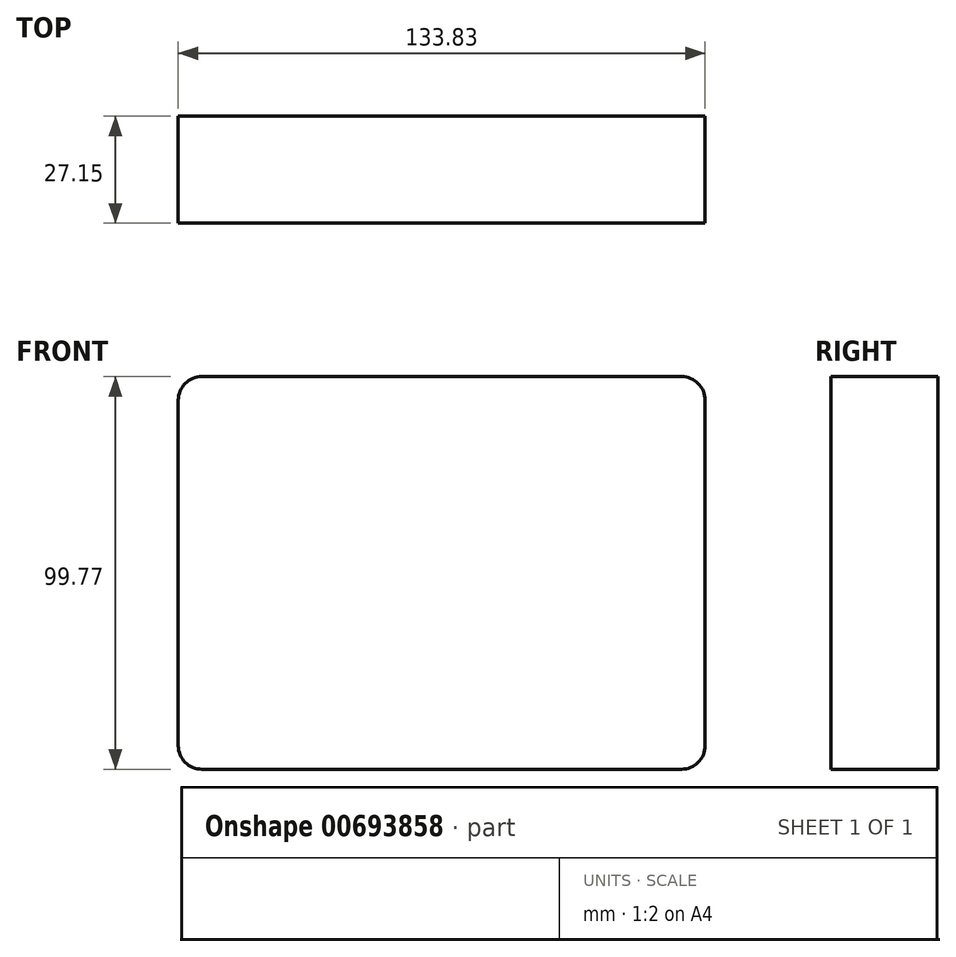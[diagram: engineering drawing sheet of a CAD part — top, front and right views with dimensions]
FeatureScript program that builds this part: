
annotation { "Feature Type Name" : "Feature", "Feature Type Description" : "" }
export const myFeature = defineFeature(function(context is Context, id is Id, definition is map)
    precondition{}
    {
        {
            var Q0;
            Q0=qCreatedBy(makeId("Front.planeOp"),FACE);
            var sketch = newSketch(context, id + "F0", { "sketchPlane" : qUnion([Q0])});
            skLineSegment(sketch, "E0.bottom", {"start": v(0, 0) * mm, "end": v(133.83, 0) * mm});
            skLineSegment(sketch, "E0.top", {"start": v(0, 99.77) * mm, "end": v(133.83, 99.77) * mm});
            skLineSegment(sketch, "E0.left", {"start": v(0, 0) * mm, "end": v(0, 99.77) * mm});
            skLineSegment(sketch, "E0.right", {"start": v(133.83, 0) * mm, "end": v(133.83, 99.77) * mm});
            skSolve(sketch);
        }
        {
            var Q0;
            Q0=makeQuery(id+"F0.imprint","IMPRINT",FACE,{"disambiguationData":[TD([[makeQuery(id+"F0.imprint","IMPRINT",EDGE,{"derivedFrom":sQuery(id+"F0.wireOp",EDGE,"E0.bottom")}),1.0]])]});
            extrude(context, id + "F1", {"entities" : qUnion([Q0]), "oppositeDirection" : true, "depth" : 27.15 * mm, "offsetDistance" : 25.4 * mm});
        }
        {
            var Q0;
            Q0=makeQuery(id+"F1.opExtrude","SWEPT_EDGE",EDGE,{"disambiguationData":[OSD([sQuery(id+"F0.wireOp",EDGE,"E0.top"),sQuery(id+"F0.wireOp",EDGE,"E0.right")])]});
            var Q1;
            Q1=makeQuery(id+"F1.opExtrude","SWEPT_EDGE",EDGE,{"disambiguationData":[OSD([sQuery(id+"F0.wireOp",EDGE,"E0.bottom"),sQuery(id+"F0.wireOp",EDGE,"E0.right")])]});
            var Q2;
            Q2=makeQuery(id+"F1.opExtrude","SWEPT_EDGE",EDGE,{"disambiguationData":[OSD([sQuery(id+"F0.wireOp",EDGE,"E0.bottom"),sQuery(id+"F0.wireOp",EDGE,"E0.left")])]});
            var Q3;
            Q3=makeQuery(id+"F1.opExtrude","SWEPT_EDGE",EDGE,{"disambiguationData":[OSD([sQuery(id+"F0.wireOp",EDGE,"E0.top"),sQuery(id+"F0.wireOp",EDGE,"E0.left")])]});
            fillet(context, id + "F2", {"entities" : qUnion([Q0, Q1, Q2, Q3]), "radius" : 6 * mm, "tangentPropagation" : true, "allowEdgeOverflow" : false});
        }
    });
